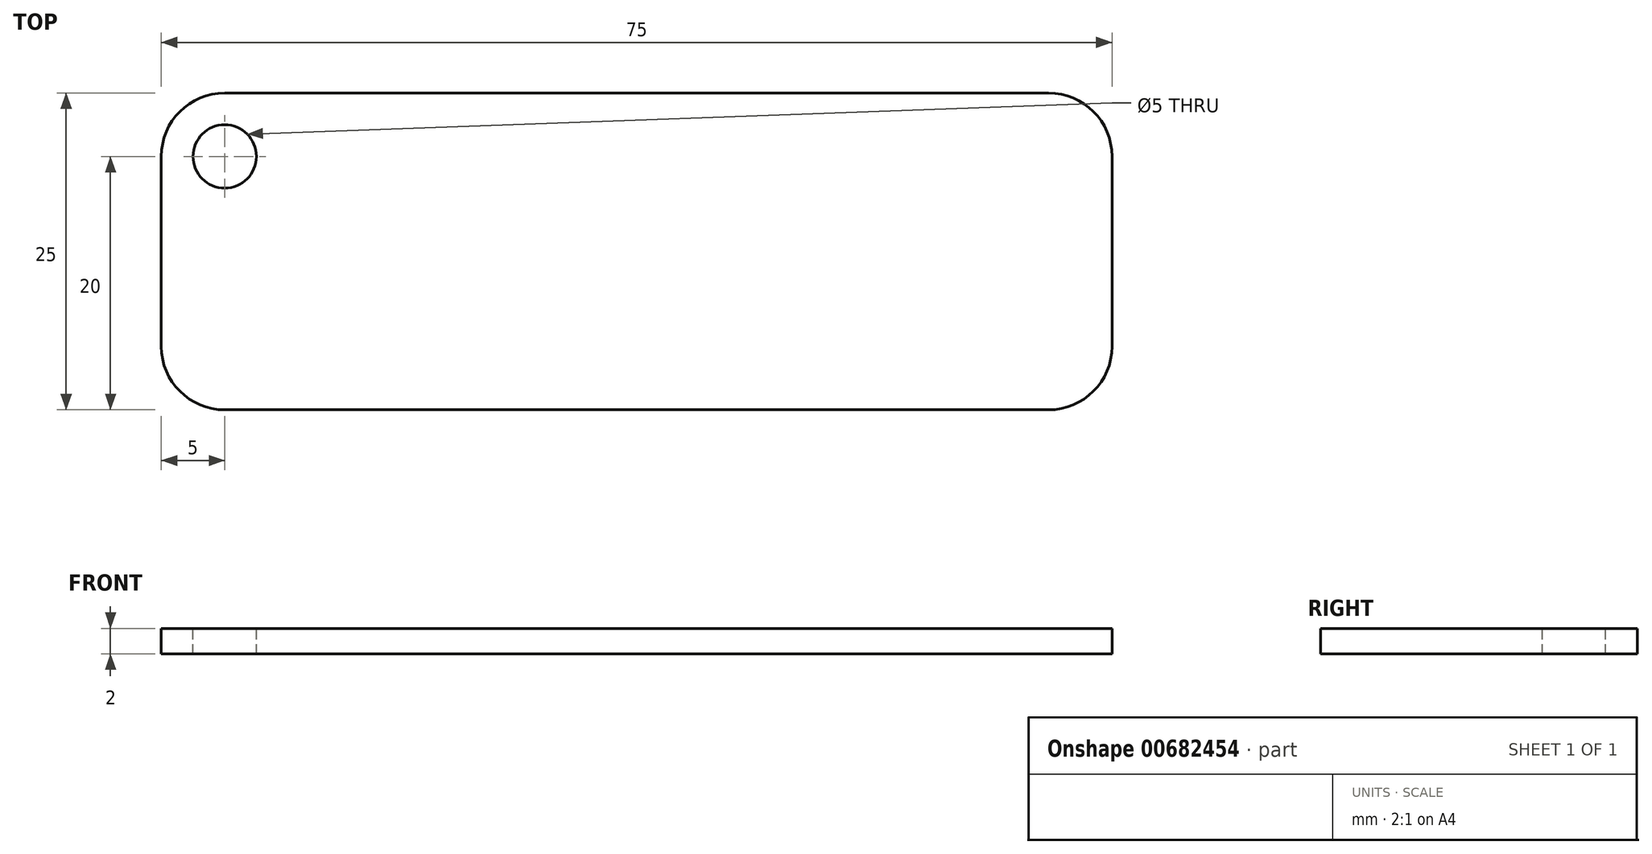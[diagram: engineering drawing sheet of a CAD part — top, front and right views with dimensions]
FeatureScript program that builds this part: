
annotation { "Feature Type Name" : "Feature", "Feature Type Description" : "" }
export const myFeature = defineFeature(function(context is Context, id is Id, definition is map)
    precondition{}
    {
        {
            var Q0;
            Q0=qCreatedBy(makeId("Top.planeOp"),FACE);
            var sketch = newSketch(context, id + "F0", { "sketchPlane" : qUnion([Q0])});
            skLineSegment(sketch, "E0.bottom", {"start": v(32.5, 12.5) * mm, "end": v(-32.5, 12.5) * mm});
            skLineSegment(sketch, "E0.top", {"start": v(32.5, -12.5) * mm, "end": v(-32.5, -12.5) * mm});
            skLineSegment(sketch, "E0.left", {"start": v(37.5, 7.5) * mm, "end": v(37.5, -7.5) * mm});
            skLineSegment(sketch, "E0.right", {"start": v(-37.5, 7.5) * mm, "end": v(-37.5, -7.5) * mm});
            skPoint(sketch, "E0.middle", {"position": v(0, 0) * mm});
            skPoint(sketch, "E1.visualSharp", {"position": v(-37.5, 12.5) * mm});
            skArc(sketch, "E1.filletArc", {"start": v(-32.5, 12.5) * mm, "mid": v(-36.04, 11.04) * mm, "end": v(-37.5, 7.5) * mm});
            skPoint(sketch, "E2.visualSharp", {"position": v(-37.5, -12.5) * mm});
            skArc(sketch, "E2.filletArc", {"start": v(-37.5, -7.5) * mm, "mid": v(-36.04, -11.04) * mm, "end": v(-32.5, -12.5) * mm});
            skPoint(sketch, "E3.visualSharp", {"position": v(37.5, -12.5) * mm});
            skArc(sketch, "E3.filletArc", {"start": v(32.5, -12.5) * mm, "mid": v(36.04, -11.04) * mm, "end": v(37.5, -7.5) * mm});
            skPoint(sketch, "E4.visualSharp", {"position": v(37.5, 12.5) * mm});
            skArc(sketch, "E4.filletArc", {"start": v(37.5, 7.5) * mm, "mid": v(36.04, 11.04) * mm, "end": v(32.5, 12.5) * mm});
            skSolve(sketch);
        }
        {
            var Q0;
            Q0=makeQuery(id+"F0.imprint","IMPRINT",FACE,{"disambiguationData":[TD([[makeQuery(id+"F0.imprint","IMPRINT",EDGE,{"derivedFrom":sQuery(id+"F0.wireOp",EDGE,"E0.bottom")}),1.0]])]});
            extrude(context, id + "F1", {"entities" : qUnion([Q0]), "depth" : 2 * mm, "offsetDistance" : 25 * mm});
        }
        {
            var Q0;
            Q0=makeQuery(id+"F1.opExtrude","CAP_FACE",FACE,{"disambiguationData":[OSD([sQuery(id+"F0.wireOp",EDGE,"E0.bottom"),sQuery(id+"F0.wireOp",EDGE,"E0.top"),sQuery(id+"F0.wireOp",EDGE,"E0.left"),sQuery(id+"F0.wireOp",EDGE,"E0.right"),sQuery(id+"F0.wireOp",EDGE,"E1.filletArc"),sQuery(id+"F0.wireOp",EDGE,"E2.filletArc"),sQuery(id+"F0.wireOp",EDGE,"E3.filletArc"),sQuery(id+"F0.wireOp",EDGE,"E4.filletArc")])],"isStart":false});
            var sketch = newSketch(context, id + "F2", { "sketchPlane" : qUnion([Q0])});
            skPoint(sketch, "E5", {"position": v(-32.5, 7.5) * mm});
            skSolve(sketch);
        }
        {
            var Q0;
            Q0=sQuery(id+"F2.wireOp",VERTEX,"E5");
            var Q1;
            Q1=makeQuery(id+"F1.opExtrude","SWEPT_BODY",BODY,{"disambiguationData":[OSD([sQuery(id+"F0.wireOp",EDGE,"E0.bottom"),sQuery(id+"F0.wireOp",EDGE,"E0.top"),sQuery(id+"F0.wireOp",EDGE,"E0.left"),sQuery(id+"F0.wireOp",EDGE,"E0.right"),sQuery(id+"F0.wireOp",EDGE,"E1.filletArc"),sQuery(id+"F0.wireOp",EDGE,"E2.filletArc"),sQuery(id+"F0.wireOp",EDGE,"E3.filletArc"),sQuery(id+"F0.wireOp",EDGE,"E4.filletArc")])]});
            hole(context, id + "F3", {"style" : HoleStyle.SIMPLE, "endStyle" : HoleEndStyle.THROUGH, "holeDiameter" : 5 * mm, "majorDiameter" : 5 * mm, "isTappedThrough" : true, "tappedDepth" : 12 * mm, "tapClearance" : 3, "locations" : qUnion([Q0]), "scope" : qUnion([Q1])});
        }
    });
